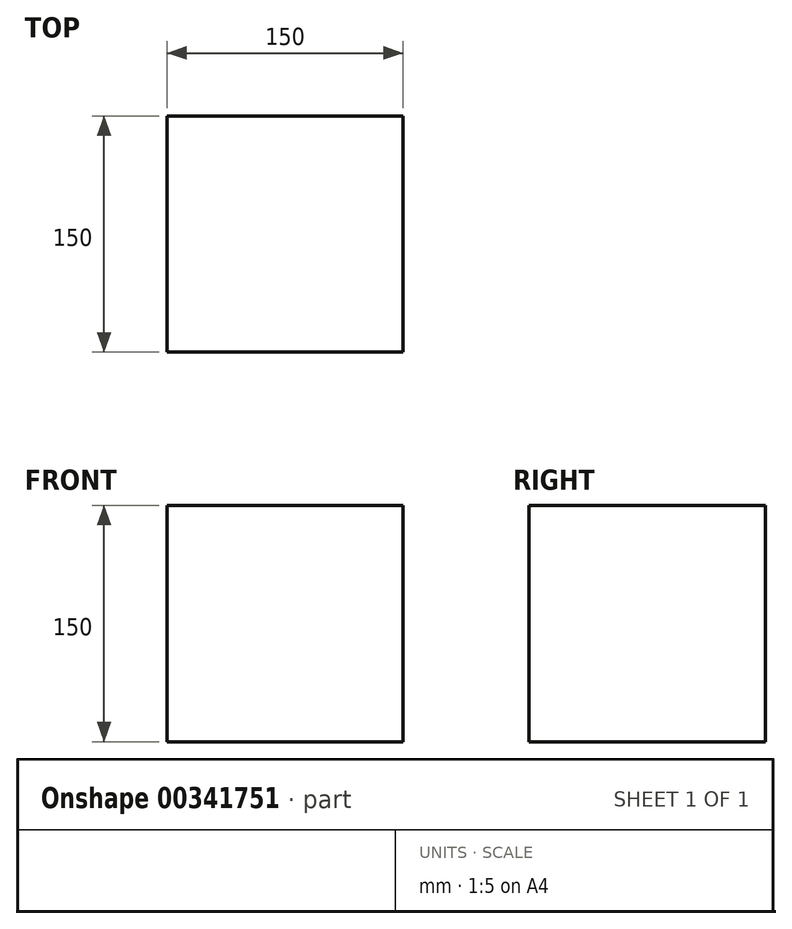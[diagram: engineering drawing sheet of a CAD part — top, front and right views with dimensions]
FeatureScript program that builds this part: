
annotation { "Feature Type Name" : "Feature", "Feature Type Description" : "" }
export const myFeature = defineFeature(function(context is Context, id is Id, definition is map)
    precondition{}
    {
        {
            var Q0;
            Q0=qCreatedBy(makeId("Top.planeOp"),FACE);
            var sketch = newSketch(context, id + "F0", { "sketchPlane" : qUnion([Q0])});
            skLineSegment(sketch, "E0.bottom", {"start": v(0, 0) * mm, "end": v(150, 0) * mm});
            skLineSegment(sketch, "E0.top", {"start": v(0, 150) * mm, "end": v(150, 150) * mm});
            skLineSegment(sketch, "E0.left", {"start": v(0, 0) * mm, "end": v(0, 150) * mm});
            skLineSegment(sketch, "E0.right", {"start": v(150, 0) * mm, "end": v(150, 150) * mm});
            skSolve(sketch);
        }
        {
            var Q0;
            Q0 = qSketchRegion(id + "F0", true);
            extrude(context, id + "F1", {"entities" : qUnion([Q0]), "depth" : 150 * mm});
        }
    });
